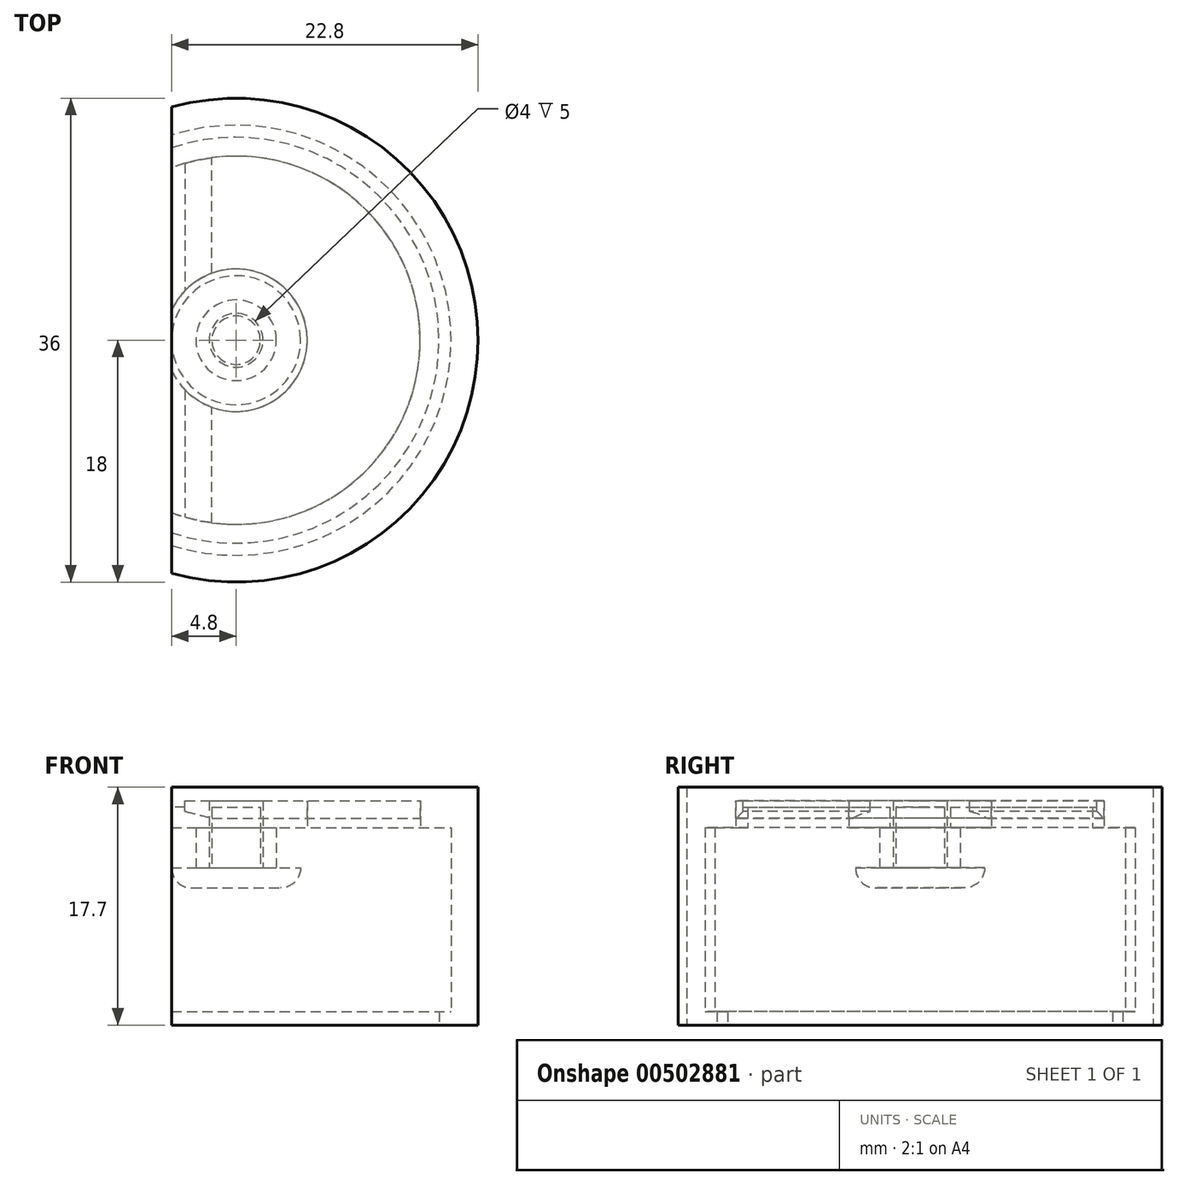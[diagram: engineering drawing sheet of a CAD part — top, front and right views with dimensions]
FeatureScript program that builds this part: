
annotation { "Feature Type Name" : "Feature", "Feature Type Description" : "" }
export const myFeature = defineFeature(function(context is Context, id is Id, definition is map)
    precondition{}
    {
        {
            var Q0;
            Q0=qCreatedBy(makeId("Right.planeOp"),FACE);
            var sketch = newSketch(context, id + "F0", { "sketchPlane" : qUnion([Q0])});
            skLineSegment(sketch, "E0", {"start": v(0, 0) * mm, "end": v(0, 78.84) * mm, "construction": true});
            skLineSegment(sketch, "E1", {"start": v(0, 17.7) * mm, "end": v(-18, 17.7) * mm});
            skLineSegment(sketch, "E2", {"start": v(-18, 17.7) * mm, "end": v(-18, 0) * mm});
            skLineSegment(sketch, "E3", {"start": v(-18, 0) * mm, "end": v(-15.1, 0) * mm});
            skLineSegment(sketch, "E4", {"start": v(-15.1, 0) * mm, "end": v(-15.1, 1) * mm});
            skLineSegment(sketch, "E5", {"start": v(-15.1, 1) * mm, "end": v(-16, 1) * mm});
            skLineSegment(sketch, "E6", {"start": v(-16, 1) * mm, "end": v(-16, 14.7) * mm});
            skLineSegment(sketch, "E7", {"start": v(-16, 14.7) * mm, "end": v(-13.7, 14.7) * mm});
            skLineSegment(sketch, "E8", {"start": v(-13.7, 14.7) * mm, "end": v(-13.7, 16.7) * mm});
            skLineSegment(sketch, "E9", {"start": v(-13.7, 16.7) * mm, "end": v(-5.3, 16.7) * mm});
            skLineSegment(sketch, "E10", {"start": v(-5.3, 16.7) * mm, "end": v(-5.3, 14.7) * mm});
            skLineSegment(sketch, "E11", {"start": v(-5.3, 14.7) * mm, "end": v(-3, 14.7) * mm});
            skLineSegment(sketch, "E12", {"start": v(-3, 14.7) * mm, "end": v(-3, 11.7) * mm});
            skLineSegment(sketch, "E13", {"start": v(0, 11.7) * mm, "end": v(-3, 11.7) * mm});
            skLineSegment(sketch, "E14", {"start": v(0, 11.7) * mm, "end": v(0, 17.7) * mm});
            skSolve(sketch);
        }
        {
            var Q0;
            Q0=makeQuery(id+"F0.imprint","IMPRINT",FACE,{"disambiguationData":[TD([[makeQuery(id+"F0.imprint","IMPRINT",EDGE,{"derivedFrom":sQuery(id+"F0.wireOp",EDGE,"E1")}),1.0]])]});
            var Q1;
            Q1=sQuery(id+"F0.wireOp",EDGE,"E0");
            revolve(context, id + "F1", {"entities" : qUnion([Q0]), "axis" : qUnion([Q1]), "revolveType" : RevolveType.FULL});
        }
        {
            var Q0;
            Q0=qCreatedBy(makeId("Front.planeOp"),FACE);
            var sketch = newSketch(context, id + "F2", { "sketchPlane" : qUnion([Q0])});
            skLineSegment(sketch, "E15.bottom", {"start": v(-18, 17.7) * mm, "end": v(-4.8, 17.7) * mm});
            skLineSegment(sketch, "E15.top", {"start": v(-18, 0) * mm, "end": v(-4.8, 0) * mm});
            skLineSegment(sketch, "E15.left", {"start": v(-18, 17.7) * mm, "end": v(-18, 0) * mm});
            skLineSegment(sketch, "E15.right", {"start": v(-4.8, 17.7) * mm, "end": v(-4.8, 0) * mm});
            skLineSegment(sketch, "E16", {"start": v(18, 17.7) * mm, "end": v(18, 0) * mm, "construction": true});
            skLineSegment(sketch, "E17.0", {"start": v(18, 17.7) * mm, "end": v(-18, 17.7) * mm, "construction": true});
            skLineSegment(sketch, "E18", {"start": v(-18, 0) * mm, "end": v(-18, 17.7) * mm, "construction": true});
            skSolve(sketch);
        }
        {
            var Q0;
            Q0=makeQuery(id+"F2.imprint","IMPRINT",FACE,{"disambiguationData":[TD([[makeQuery(id+"F2.imprint","IMPRINT",EDGE,{"derivedFrom":sQuery(id+"F2.wireOp",EDGE,"E15.bottom")}),-1.0]])]});
            extrude(context, id + "F3", {"entities" : qUnion([Q0]), "operationType" : NewBodyOperationType.REMOVE, "depth" : 25 * mm, "hasSecondDirection" : true, "secondDirectionOppositeDirection" : true, "secondDirectionDepth" : 25 * mm, "offsetDistance" : 25 * mm});
        }
        {
            var Q0;
            Q0=makeQuery(id+"F1.opRevolve","SWEPT_FACE",FACE,{"disambiguationData":[OSD([sQuery(id+"F0.wireOp",EDGE,"E9")])]});
            var sketch = newSketch(context, id + "F4", { "sketchPlane" : qUnion([Q0])});
            skLineSegment(sketch, "E19.0", {"start": v(-4.8, 12.83) * mm, "end": v(-4.8, 2.25) * mm});
            skLineSegment(sketch, "E20.0", {"start": v(-4.8, -2.25) * mm, "end": v(-4.8, -12.83) * mm});
            skLineSegment(sketch, "E21.0", {"start": v(-3.8, 14.61) * mm, "end": v(-3.8, 3.7) * mm});
            skLineSegment(sketch, "E22.0", {"start": v(-3.8, -3.7) * mm, "end": v(-3.8, -14.61) * mm});
            skArc(sketch, "E23.0", {"start": v(-4.8, -14.32) * mm, "mid": v(15.1, 0) * mm, "end": v(-4.8, 14.32) * mm});
            skArc(sketch, "E24.0", {"start": v(-4.8, -2.25) * mm, "mid": v(5.3, 0) * mm, "end": v(-4.8, 2.25) * mm});
            skSolve(sketch);
        }
        {
            var Q0;
            {var subQ0=sQuery(id+"F4.wireOp",EDGE,"E19.0");Q0=makeQuery(id+"F4.imprint","IMPRINT",FACE,{"disambiguationData":[TD([[makeQuery(id+"F4.imprint","IMPRINT",EDGE,{"derivedFrom":subQ0}),1.0]])]});}
            var Q1;
            {var subQ0=sQuery(id+"F4.wireOp",EDGE,"E20.0");Q1=makeQuery(id+"F4.imprint","IMPRINT",FACE,{"disambiguationData":[TD([[makeQuery(id+"F4.imprint","IMPRINT",EDGE,{"derivedFrom":subQ0}),1.0]])]});}
            extrude(context, id + "F5", {"entities" : qUnion([Q0, Q1]), "operationType" : NewBodyOperationType.ADD, "depth" : .5 * mm});
        }
        {
            var Q0;
            Q0=makeQuery(id+"F1.opRevolve","SWEPT_FACE",FACE,{"disambiguationData":[OSD([sQuery(id+"F0.wireOp",EDGE,"E13")])]});
            var sketch = newSketch(context, id + "F6", { "sketchPlane" : qUnion([Q0])});
            skCircle(sketch, "E25.0", {"center": v(0, 0) * mm, "radius": 2 * mm});
            skSolve(sketch);
        }
        {
            var Q0;
            Q0=makeQuery(id+"F6.imprint","IMPRINT",FACE,{"disambiguationData":[TD([[makeQuery(id+"F6.imprint","IMPRINT",EDGE,{"derivedFrom":sQuery(id+"F6.wireOp",EDGE,"E25.0")}),1.0]])]});
            extrude(context, id + "F7", {"entities" : qUnion([Q0]), "operationType" : NewBodyOperationType.REMOVE, "oppositeDirection" : true, "depth" : 5 * mm, "offsetDistance" : 25 * mm});
        }
        {
            var Q0;
            Q0=makeQuery(id+"F1.opRevolve","SWEPT_FACE",FACE,{"disambiguationData":[OSD([sQuery(id+"F0.wireOp",EDGE,"E13")])]});
            var sketch = newSketch(context, id + "F8", { "sketchPlane" : qUnion([Q0])});
            skCircle(sketch, "E26.0", {"center": v(0, 0) * mm, "radius": 1.8 * mm});
            skSolve(sketch);
        }
        {
            var Q0;
            Q0=makeQuery(id+"F8.imprint","IMPRINT",FACE,{"disambiguationData":[TD([[makeQuery(id+"F8.imprint","IMPRINT",EDGE,{"derivedFrom":sQuery(id+"F8.wireOp",EDGE,"E26.0")}),1.0]])]});
            extrude(context, id + "F9", {"entities" : qUnion([Q0]), "oppositeDirection" : true, "depth" : 4.5 * mm, "offsetDistance" : 25 * mm});
        }
        {
            var Q0;
            Q0=makeQuery(id+"F9.opExtrude","CAP_FACE",FACE,{"disambiguationData":[OSD([sQuery(id+"F8.wireOp",EDGE,"E26.0")])],"isStart":true});
            var sketch = newSketch(context, id + "F10", { "sketchPlane" : qUnion([Q0])});
            skCircle(sketch, "E27.0", {"center": v(0, 0) * mm, "radius": 4.8 * mm});
            skSolve(sketch);
        }
        {
            var Q0;
            Q0=makeQuery(id+"F10.imprint","IMPRINT",FACE,{"disambiguationData":[TD([[makeQuery(id+"F10.imprint","IMPRINT",EDGE,{"derivedFrom":makeQuery(id+"F9.opExtrude","CAP_EDGE",EDGE,{"disambiguationData":[OSD([sQuery(id+"F8.wireOp",EDGE,"E26.0")])],"isStart":true})}),1.0]])]});
            var Q1;
            Q1=makeQuery(id+"F10.imprint","IMPRINT",FACE,{"disambiguationData":[TD([[makeQuery(id+"F10.imprint","IMPRINT",EDGE,{"derivedFrom":sQuery(id+"F10.wireOp",EDGE,"E27.0")}),1.0]])]});
            extrude(context, id + "F11", {"entities" : qUnion([Q0, Q1]), "operationType" : NewBodyOperationType.ADD, "depth" : 1.5 * mm, "offsetDistance" : 25 * mm});
        }
        {
            var Q0;
            Q0=makeQuery(id+"F11.opExtrude","CAP_EDGE",EDGE,{"disambiguationData":[OSD([sQuery(id+"F10.wireOp",EDGE,"E27.0")])],"isStart":false});
            fillet(context, id + "F12", {"entities" : qUnion([Q0]), "radius" : 1.5 * mm, "tangentPropagation" : true, "allowEdgeOverflow" : false});
        }
        {
            var Q0;
            Q0=makeQuery(id+"F1.opRevolve","SWEPT_FACE",FACE,{"disambiguationData":[OSD([sQuery(id+"F0.wireOp",EDGE,"E9")])]});
            var sketch = newSketch(context, id + "F13", { "sketchPlane" : qUnion([Q0])});
            skArc(sketch, "E28.0", {"start": v(-3.8, -13.16) * mm, "mid": v(13.7, 0) * mm, "end": v(-3.8, 13.16) * mm});
            skArc(sketch, "E29.0", {"start": v(-3.8, -3.7) * mm, "mid": v(5.3, 0) * mm, "end": v(-3.8, 3.7) * mm});
            skLineSegment(sketch, "E30.0", {"start": v(-3.8, 13.16) * mm, "end": v(-3.8, 3.7) * mm});
            skLineSegment(sketch, "E31.0", {"start": v(-3.8, -3.7) * mm, "end": v(-3.8, -13.16) * mm});
            skSolve(sketch);
        }
        {
            var Q0;
            Q0 = qSketchRegion(id + "F13", true);
            extrude(context, id + "F14", {"entities" : qUnion([Q0]), "depth" : 1.3 * mm, "offsetDistance" : 25 * mm});
        }
        {
            var Q0;
            Q0=makeQuery(id+"F14.opExtrude","CAP_EDGE",EDGE,{"disambiguationData":[OSD([sQuery(id+"F13.wireOp",EDGE,"E31.0")])],"isStart":false});
            var Q1;
            Q1=makeQuery(id+"F14.opExtrude","CAP_EDGE",EDGE,{"disambiguationData":[OSD([sQuery(id+"F13.wireOp",EDGE,"E30.0")])],"isStart":false});
            chamfer(context, id + "F15", {"entities" : qUnion([Q0, Q1]), "chamferType" : ChamferType.TWO_OFFSETS, "width1" : 2 * mm, "oppositeDirection" : false, "width2" : .5 * mm, "tangentPropagation" : true});
        }
    });
